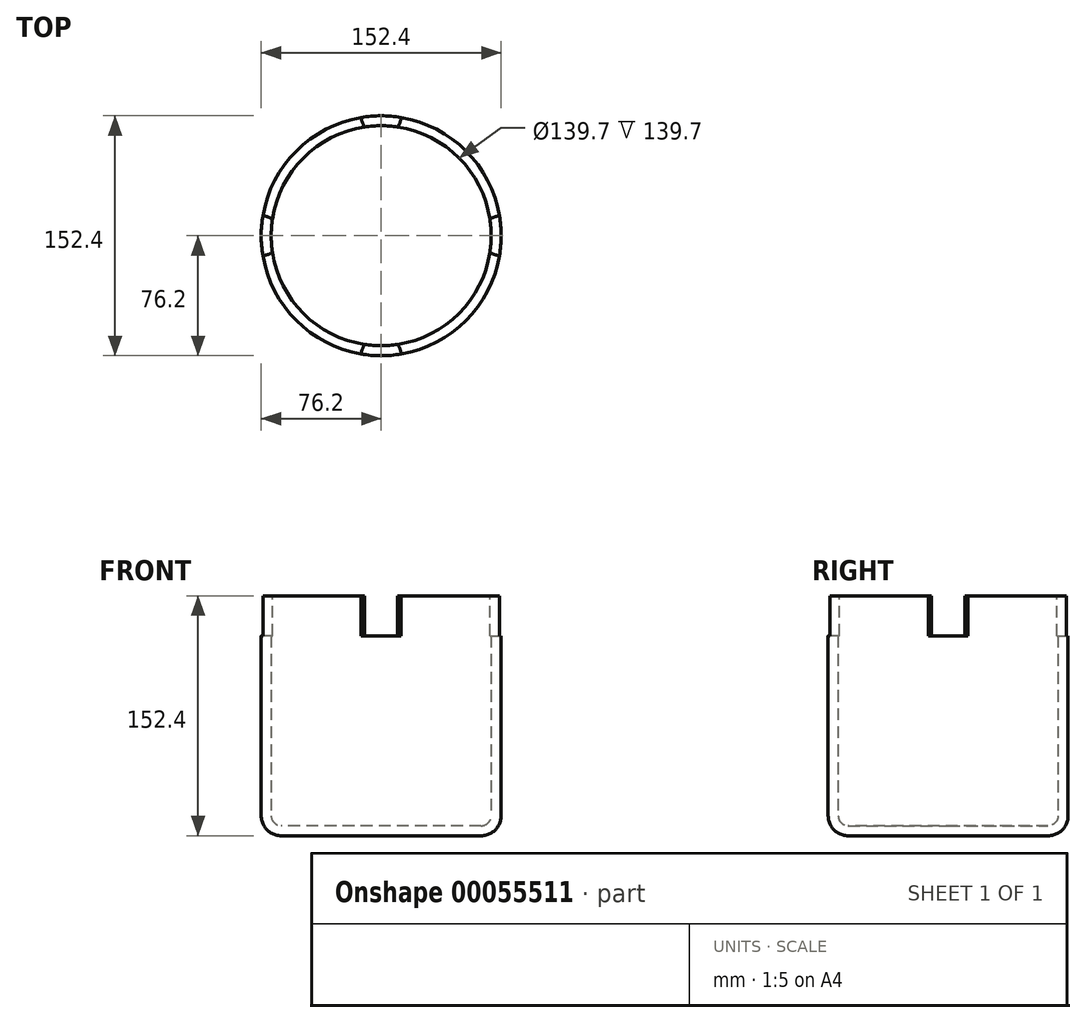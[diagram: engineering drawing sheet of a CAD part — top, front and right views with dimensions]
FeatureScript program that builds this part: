
annotation { "Feature Type Name" : "Feature", "Feature Type Description" : "" }
export const myFeature = defineFeature(function(context is Context, id is Id, definition is map)
    precondition{}
    {
        {
            var Q0;
            Q0=qCreatedBy(makeId("Top.planeOp"),FACE);
            var sketch = newSketch(context, id + "F0", { "sketchPlane" : qUnion([Q0])});
            skCircle(sketch, "E0", {"center": v(0, 0) * mm, "radius": 76.2 * mm});
            skSolve(sketch);
        }
        {
            var Q0;
            Q0=makeQuery(id+"F0.imprint","IMPRINT",FACE,{"disambiguationData":[TD([[makeQuery(id+"F0.imprint","IMPRINT",EDGE,{"derivedFrom":sQuery(id+"F0.wireOp",EDGE,"E0")}),1.0]])]});
            extrude(context, id + "F1", {"entities" : qUnion([Q0]), "depth" : 152.4 * mm});
        }
        {
            var Q0;
            Q0=makeQuery(id+"F1.opExtrude","CAP_EDGE",EDGE,{"disambiguationData":[OSD([sQuery(id+"F0.wireOp",EDGE,"E0")])],"isStart":true});
            fillet(context, id + "F2", {"entities" : qUnion([Q0]), "radius" : 12.7 * mm, "tangentPropagation" : true, "allowEdgeOverflow" : false});
        }
        {
            var Q0;
            Q0=makeQuery(id+"F1.opExtrude","CAP_FACE",FACE,{"disambiguationData":[OSD([sQuery(id+"F0.wireOp",EDGE,"E0")])],"isStart":false});
            shell(context, id + "F3", {"entities" : qUnion([Q0]), "thickness" : 6.35 * mm});
        }
        {
            var Q0;
            Q0=makeQuery(id+"F1.opExtrude","CAP_FACE",FACE,{"disambiguationData":[OSD([sQuery(id+"F0.wireOp",EDGE,"E0")])],"isStart":false});
            var sketch = newSketch(context, id + "F4", { "sketchPlane" : qUnion([Q0])});
            skCircle(sketch, "E1", {"center": v(0, 76.2) * mm, "radius": 12.7 * mm});
            skCircle(sketch, "E2.1.0", {"center": v(-76.2, 0) * mm, "radius": 12.7 * mm});
            skCircle(sketch, "E2.2.0", {"center": v(0, -76.2) * mm, "radius": 12.7 * mm});
            skCircle(sketch, "E2.3.0", {"center": v(76.2, 0) * mm, "radius": 12.7 * mm});
            skPoint(sketch, "E2.center", {"position": v(0, 0) * mm});
            skSolve(sketch);
        }
        {
            var Q0;
            Q0 = qSketchRegion(id + "F4", true);
            extrude(context, id + "F5", {"entities" : qUnion([Q0]), "operationType" : NewBodyOperationType.REMOVE, "oppositeDirection" : true, "depth" : 25.4 * mm});
        }
    });
